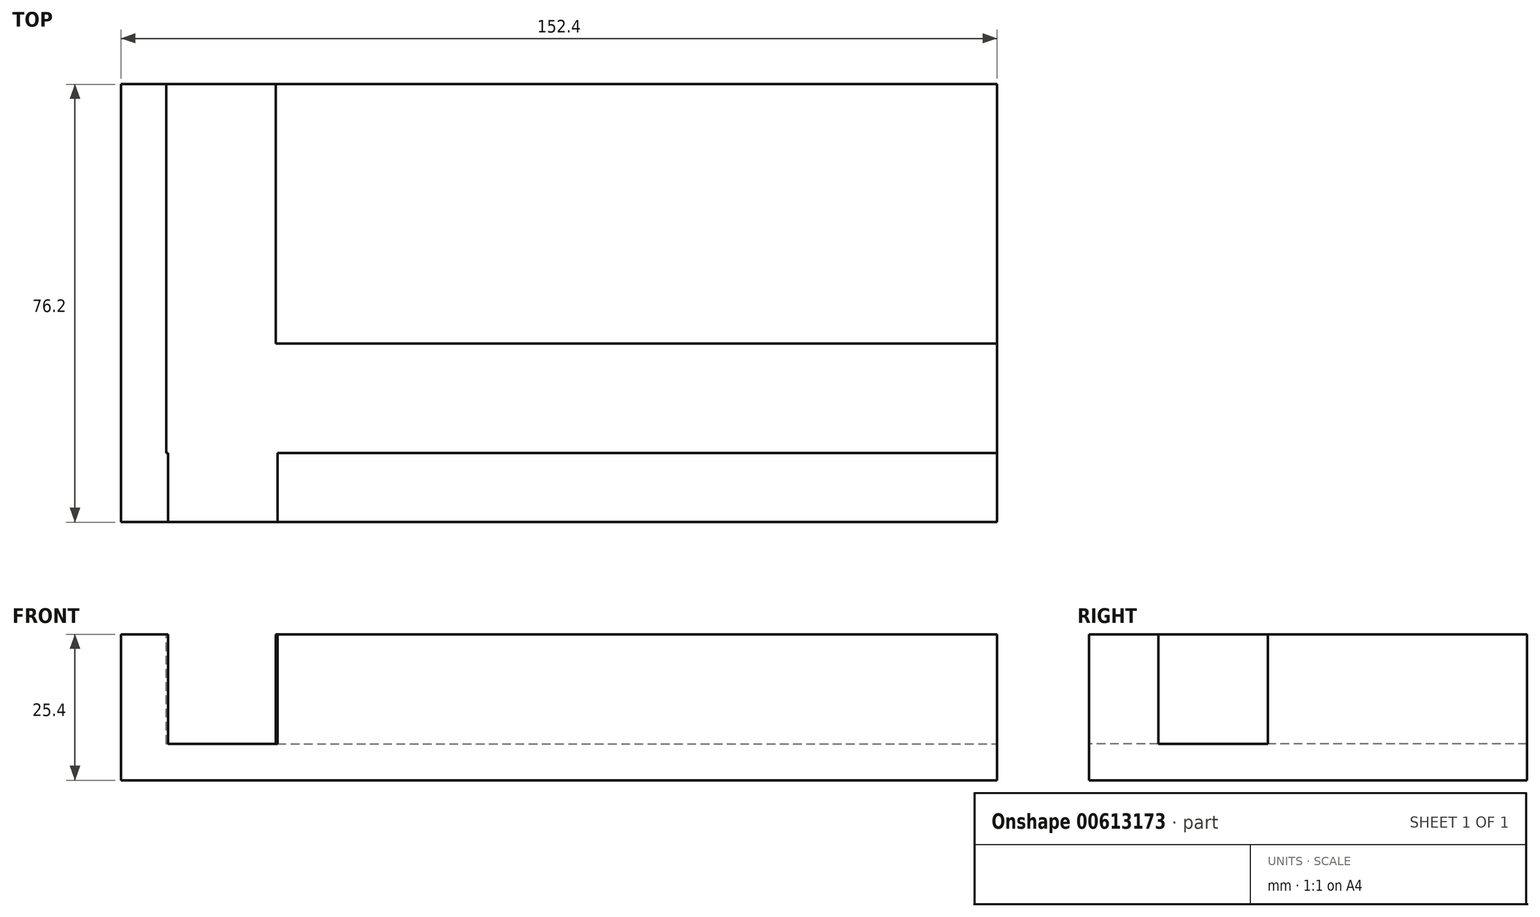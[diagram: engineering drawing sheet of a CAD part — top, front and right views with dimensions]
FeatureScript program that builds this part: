
annotation { "Feature Type Name" : "Feature", "Feature Type Description" : "" }
export const myFeature = defineFeature(function(context is Context, id is Id, definition is map)
    precondition{}
    {
        {
            var Q0;
            Q0=qCreatedBy(makeId("Top.planeOp"),FACE);
            var sketch = newSketch(context, id + "F0", { "sketchPlane" : qUnion([Q0])});
            skLineSegment(sketch, "E0.bottom", {"start": v(-52.12, 31.2) * mm, "end": v(100.28, 31.2) * mm});
            skLineSegment(sketch, "E0.top", {"start": v(-52.12, -45) * mm, "end": v(100.28, -45) * mm});
            skLineSegment(sketch, "E0.left", {"start": v(-52.12, 31.2) * mm, "end": v(-52.12, -45) * mm});
            skLineSegment(sketch, "E0.right", {"start": v(100.28, 31.2) * mm, "end": v(100.28, -45) * mm});
            skSolve(sketch);
        }
        {
            var Q0;
            Q0=qSketchRegion(id+"F0",true);
            extrude(context, id + "F1", {"entities" : qUnion([Q0]), "depth" : 25.4 * mm, "offsetDistance" : 25.4 * mm});
        }
        {
            var Q0;
            Q0=makeQuery(id+"F1.opExtrude","CAP_FACE",FACE,{"disambiguationData":[OSD([sQuery(id+"F0.wireOp",EDGE,"E0.bottom"),sQuery(id+"F0.wireOp",EDGE,"E0.top"),sQuery(id+"F0.wireOp",EDGE,"E0.left"),sQuery(id+"F0.wireOp",EDGE,"E0.right")])],"isStart":false});
            var sketch = newSketch(context, id + "F2", { "sketchPlane" : qUnion([Q0])});
            skLineSegment(sketch, "E1", {"start": v(-44.23, 31.2) * mm, "end": v(-44.23, -32.95) * mm});
            skLineSegment(sketch, "E2", {"start": v(-44.23, -32.95) * mm, "end": v(100.28, -32.95) * mm});
            skLineSegment(sketch, "E3", {"start": v(100.28, -32.95) * mm, "end": v(100.28, -13.9) * mm});
            skLineSegment(sketch, "E4", {"start": v(100.28, -13.9) * mm, "end": v(-25.18, -13.9) * mm});
            skLineSegment(sketch, "E5", {"start": v(-25.18, -13.9) * mm, "end": v(-25.18, 31.2) * mm});
            skLineSegment(sketch, "E6", {"start": v(-25.18, 31.2) * mm, "end": v(-44.23, 31.2) * mm});
            skSolve(sketch);
        }
        {
            var Q0;
            Q0=qSketchRegion(id+"F2",true);
            extrude(context, id + "F3", {"entities" : qUnion([Q0]), "operationType" : NewBodyOperationType.REMOVE, "oppositeDirection" : true, "depth" : 19.05 * mm, "offsetDistance" : 25.4 * mm});
        }
        {
            var Q0;
            Q0=makeQuery(id+"F1.opExtrude","SWEPT_FACE",FACE,{"disambiguationData":[OSD([sQuery(id+"F0.wireOp",EDGE,"E0.top")])]});
            var sketch = newSketch(context, id + "F4", { "sketchPlane" : qUnion([Q0])});
            skLineSegment(sketch, "E7.bottom", {"start": v(-43.94, 25.4) * mm, "end": v(-24.89, 25.4) * mm});
            skLineSegment(sketch, "E7.top", {"start": v(-43.94, 6.35) * mm, "end": v(-24.89, 6.35) * mm});
            skLineSegment(sketch, "E7.left", {"start": v(-43.94, 25.4) * mm, "end": v(-43.94, 6.35) * mm});
            skLineSegment(sketch, "E7.right", {"start": v(-24.89, 25.4) * mm, "end": v(-24.89, 6.35) * mm});
            skSolve(sketch);
        }
        {
            var Q0;
            Q0=qSketchRegion(id+"F4",true);
            extrude(context, id + "F5", {"entities" : qUnion([Q0]), "operationType" : NewBodyOperationType.REMOVE, "oppositeDirection" : true, "depth" : 12.2 * mm, "offsetDistance" : 25.4 * mm});
        }
    });
